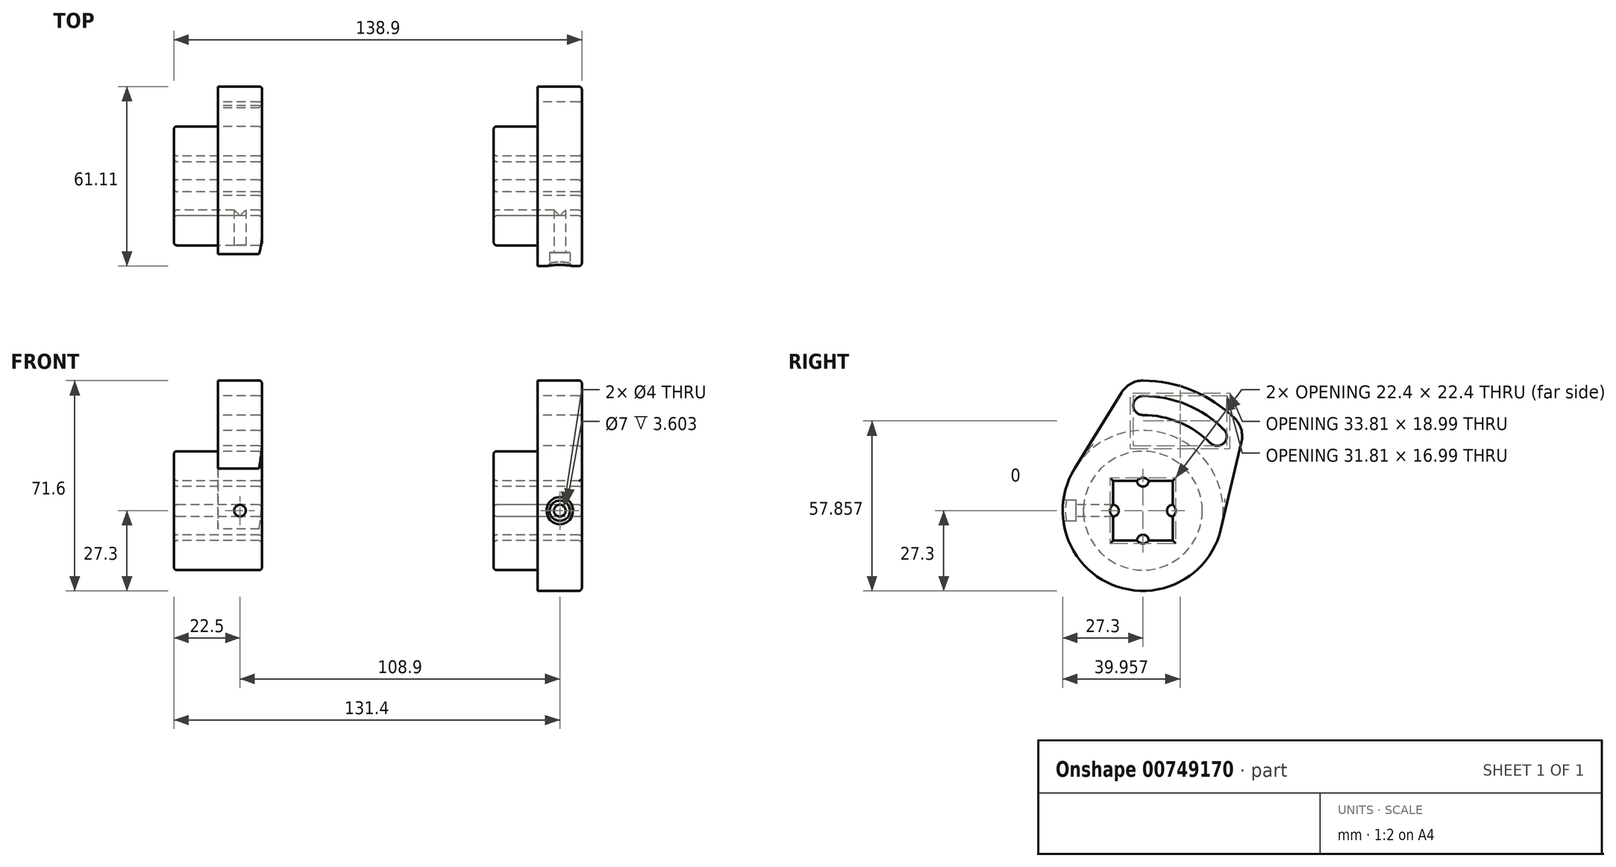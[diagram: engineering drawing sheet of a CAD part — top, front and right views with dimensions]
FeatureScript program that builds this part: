
annotation { "Feature Type Name" : "Feature", "Feature Type Description" : "" }
export const myFeature = defineFeature(function(context is Context, id is Id, definition is map)
    precondition{}
    {
        {
            var Q0;
            Q0=qCreatedBy(makeId("Right.planeOp"),FACE);
            var sketch = newSketch(context, id + "F0", { "sketchPlane" : qUnion([Q0])});
            skPoint(sketch, "E0.middle", {"position": v(0, 0) * mm});
            skCircle(sketch, "E1", {"center": v(0, 0) * mm, "radius": 20.25 * mm});
            skSolve(sketch);
        }
        {
            var Q0;
            Q0=makeQuery(id+"F0.imprint","IMPRINT",FACE,{"disambiguationData":[TD([[makeQuery(id+"F0.imprint","IMPRINT",EDGE,{"derivedFrom":sQuery(id+"F0.wireOp",EDGE,"E1")}),1.0]])]});
            extrude(context, id + "F1", {"entities" : qUnion([Q0]), "depth" : 15 * mm, "offsetDistance" : 25 * mm});
        }
        {
            var Q0;
            Q0=makeQuery(id+"F1.opExtrude","CAP_FACE",FACE,{"disambiguationData":[OSD([sQuery(id+"F0.wireOp",EDGE,"E1")])],"isStart":false});
            var sketch = newSketch(context, id + "F2", { "sketchPlane" : qUnion([Q0])});
            skPoint(sketch, "E2.center", {"position": v(0, 0) * mm});
            skArc(sketch, "E3", {"start": v(-23.23, 14.34) * mm, "mid": v(-10.45, -25.22) * mm, "end": v(26.57, -6.3) * mm});
            skArc(sketch, "E4", {"start": v(0, 44.3) * mm, "mid": v(-4.14, 43.22) * mm, "end": v(-7.23, 40.26) * mm});
            skArc(sketch, "E5", {"start": v(0, 39.05) * mm, "mid": v(-3.25, 35.8) * mm, "end": v(0, 32.55) * mm});
            skArc(sketch, "E6.1.0", {"start": v(33.59, 23.36) * mm, "mid": v(33.5, 27.63) * mm, "end": v(31.32, 31.32) * mm});
            skArc(sketch, "E6.1.1", {"start": v(23.02, 23.02) * mm, "mid": v(27.61, 23.02) * mm, "end": v(27.61, 27.61) * mm});
            skLineSegment(sketch, "E6.anchor1", {"start": v(0, 0) * mm, "end": v(0, 35.8) * mm, "construction": true});
            skLineSegment(sketch, "E6.anchor2", {"start": v(0, 0) * mm, "end": v(25.31, 25.31) * mm, "construction": true});
            skArc(sketch, "E7", {"start": v(0, 44.3) * mm, "mid": v(16.95, 40.93) * mm, "end": v(31.32, 31.32) * mm});
            skLineSegment(sketch, "E8", {"start": v(-7.23, 40.26) * mm, "end": v(-23.23, 14.34) * mm});
            skLineSegment(sketch, "E9", {"start": v(33.59, 23.36) * mm, "end": v(26.57, -6.3) * mm});
            skArc(sketch, "E10", {"start": v(0, 39.05) * mm, "mid": v(14.94, 36.08) * mm, "end": v(27.61, 27.61) * mm});
            skArc(sketch, "E11", {"start": v(0, 32.55) * mm, "mid": v(12.46, 30.07) * mm, "end": v(23.02, 23.02) * mm});
            skSolve(sketch);
        }
        {
            var Q0;
            Q0=makeQuery(id+"F2.imprint","IMPRINT",FACE,{"disambiguationData":[TD([[makeQuery(id+"F2.imprint","IMPRINT",EDGE,{"derivedFrom":sQuery(id+"F2.wireOp",EDGE,"mr3UQ9HW-HN6N-brF4-2AbY-BRYGOn4Xsbo6")}),1.0]])]});
            var Q1;
            Q1=makeQuery(id+"F2.imprint","IMPRINT",FACE,{"disambiguationData":[TD([[makeQuery(id+"F2.imprint","IMPRINT",EDGE,{"derivedFrom":makeQuery(id+"F1.opExtrude","CAP_EDGE",EDGE,{"disambiguationData":[OSD([sQuery(id+"F0.wireOp",EDGE,"E1")])],"isStart":false})}),1.0]])]});
            extrude(context, id + "F3", {"entities" : qUnion([Q0, Q1]), "operationType" : NewBodyOperationType.ADD, "depth" : 15 * mm, "offsetDistance" : 25 * mm});
        }
        {
            var Q0;
            Q0=makeQuery(id+"F1.opExtrude","CAP_FACE",FACE,{"disambiguationData":[OSD([sQuery(id+"F0.wireOp",EDGE,"E1")])],"isStart":true});
            var sketch = newSketch(context, id + "F4", { "sketchPlane" : qUnion([Q0])});
            skLineSegment(sketch, "E12.bottom", {"start": v(10.2, -10.2) * mm, "end": v(-10.2, -10.2) * mm});
            skLineSegment(sketch, "E12.top", {"start": v(10.2, 10.2) * mm, "end": v(-10.2, 10.2) * mm});
            skLineSegment(sketch, "E12.left", {"start": v(10.2, -10.2) * mm, "end": v(10.2, 10.2) * mm});
            skLineSegment(sketch, "E12.right", {"start": v(-10.2, -10.2) * mm, "end": v(-10.2, 10.2) * mm});
            skPoint(sketch, "E12.middle", {"position": v(0, 0) * mm});
            skArc(sketch, "E13", {"start": v(-2, 10.2) * mm, "mid": v(0, 8.2) * mm, "end": v(2, 10.2) * mm});
            skPoint(sketch, "E13.centerSnap0", {"position": v(0, 10.2) * mm});
            skArc(sketch, "E14.1.0", {"start": v(-10.2, -2) * mm, "mid": v(-8.2, 0) * mm, "end": v(-10.2, 2) * mm});
            skArc(sketch, "E14.2.0", {"start": v(2, -10.2) * mm, "mid": v(0, -8.2) * mm, "end": v(-2, -10.2) * mm});
            skArc(sketch, "E14.3.0", {"start": v(10.2, 2) * mm, "mid": v(8.2, 0) * mm, "end": v(10.2, -2) * mm});
            skSolve(sketch);
        }
        {
            var Q0;
            {var subQ0=sQuery(id+"F4.wireOp",EDGE,"E13");Q0=makeQuery(id+"F4.imprint","IMPRINT",FACE,{"disambiguationData":[TD([[makeQuery(id+"F4.imprint","IMPRINT",EDGE,{"derivedFrom":subQ0}),-1.0]])]});}
            extrude(context, id + "F5", {"entities" : qUnion([Q0]), "operationType" : NewBodyOperationType.REMOVE, "endBound" : BoundingType.UP_TO_NEXT, "oppositeDirection" : true, "depth" : 25 * mm, "offsetDistance" : 25 * mm});
        }
        {
            var Q0;
            Q0=makeQuery(id+"F2.imprint","IMPRINT",FACE,{"disambiguationData":[TD([[makeQuery(id+"F2.imprint","IMPRINT",EDGE,{"derivedFrom":sQuery(id+"F2.wireOp",EDGE,"E3")}),1.0]])]});
            var Q1;
            Q1=makeQuery(id+"F3.opExtrude","CAP_FACE",FACE,{"disambiguationData":[OSD([sQuery(id+"F0.wireOp",EDGE,"E1")])],"isStart":false});
            extrude(context, id + "F6", {"entities" : qUnion([Q0]), "operationType" : NewBodyOperationType.ADD, "endBound" : BoundingType.UP_TO_SURFACE, "depth" : 25 * mm, "endBoundEntityFace" : qUnion([Q1]), "offsetDistance" : 25 * mm});
        }
        {
            var Q0;
            Q0=qCreatedBy(makeId("Front.planeOp"),FACE);
            cPlane(context, id + "F7", {"entities" : qUnion([Q0]), "cplaneType" : CPlaneType.OFFSET, "offset" : 27.7 * mm, "width" : 150 * mm, "height" : 150 * mm});
        }
        {
            var Q0;
            Q0=qCreatedBy(id+"F7.planeOp",FACE);
            var sketch = newSketch(context, id + "F8", { "sketchPlane" : qUnion([Q0])});
            skCircle(sketch, "E15", {"center": v(22.5, 0) * mm, "radius": 2 * mm});
            skLineSegment(sketch, "E16", {"start": v(30, -27.3) * mm, "end": v(15, -27.3) * mm, "construction": true});
            skPoint(sketch, "E17", {"position": v(22.5, -27.3) * mm});
            skCircle(sketch, "E18", {"center": v(22.5, 0) * mm, "radius": 3.5 * mm});
            skSolve(sketch);
        }
        {
            var Q0;
            Q0=makeQuery(id+"F8.imprint","IMPRINT",FACE,{"disambiguationData":[TD([[makeQuery(id+"F8.imprint","IMPRINT",EDGE,{"derivedFrom":sQuery(id+"F8.wireOp",EDGE,"E15")}),1.0]])]});
            extrude(context, id + "F9", {"entities" : qUnion([Q0]), "operationType" : NewBodyOperationType.REMOVE, "oppositeDirection" : true, "depth" : 25 * mm, "offsetDistance" : 25 * mm});
        }
        {
            var Q0;
            Q0=makeQuery(id+"F8.imprint","IMPRINT",FACE,{"disambiguationData":[TD([[makeQuery(id+"F8.imprint","IMPRINT",EDGE,{"derivedFrom":sQuery(id+"F8.wireOp",EDGE,"E15")}),-1.0]])]});
            extrude(context, id + "F10", {"entities" : qUnion([Q0]), "operationType" : NewBodyOperationType.REMOVE, "oppositeDirection" : true, "depth" : 5 * mm, "offsetDistance" : 25 * mm});
        }
        {
            var Q0;
            Q0=makeQuery(id+"F10.boolean.opBoolean","INTERSECT",EDGE,{"derivedFrom":[makeQuery(id+"F6.opExtrude","SWEPT_FACE",FACE,{"disambiguationData":[OSD([sQuery(id+"F2.wireOp",EDGE,"E3")])]}),makeQuery(id+"F10.opExtrude","SWEPT_FACE",FACE,{"disambiguationData":[OSD([sQuery(id+"F8.wireOp",EDGE,"E18")])]})]});
            fillet(context, id + "F11", {"entities" : qUnion([Q0]), "radius" : 1 * mm, "tangentPropagation" : true, "allowEdgeOverflow" : false});
        }
        {
            var Q0;
            Q0=makeQuery(id+"F1.opExtrude","SWEPT_BODY",BODY,{"disambiguationData":[OSD([sQuery(id+"F0.wireOp",EDGE,"E1")])]});
            transform(context, id + "F12", {"entities" : qUnion([Q0]), "transformType" : TransformType.TRANSLATION_3D, "dx" : -108.9 * mm, "dy" : 0 * mm, "dz" : 0 * mm, "makeCopy" : true});
        }
        {
            var Q0;
            Q0=makeQuery(id+"F12.opPattern","COPY",FACE,{"derivedFrom":makeQuery(id+"F6.opExtrude","CAP_FACE",FACE,{"disambiguationData":[OSD([sQuery(id+"F0.wireOp",EDGE,"E1"),sQuery(id+"F2.wireOp",EDGE,"E3"),sQuery(id+"F2.wireOp",EDGE,"E4"),sQuery(id+"F2.wireOp",EDGE,"E5"),sQuery(id+"F2.wireOp",EDGE,"E6.1.0"),sQuery(id+"F2.wireOp",EDGE,"E6.1.1"),sQuery(id+"F2.wireOp",EDGE,"E7"),sQuery(id+"F2.wireOp",EDGE,"E8"),sQuery(id+"F2.wireOp",EDGE,"E9"),sQuery(id+"F2.wireOp",EDGE,"E10"),sQuery(id+"F2.wireOp",EDGE,"E11")])],"isStart":true}),"instanceName":"1"});
            var sketch = newSketch(context, id + "F13", { "sketchPlane" : qUnion([Q0])});
            skArc(sketch, "E19.0", {"start": v(23.23, 14.34) * mm, "mid": v(10.45, -25.22) * mm, "end": v(-26.57, -6.3) * mm});
            skArc(sketch, "E20", {"start": v(-26.57, -6.3) * mm, "mid": v(-10.45, 25.22) * mm, "end": v(23.23, 14.34) * mm});
            skSolve(sketch);
        }
        {
            var Q0;
            Q0=makeQuery(id+"F13.imprint","IMPRINT",FACE,{"disambiguationData":[TD([[makeQuery(id+"F13.imprint","IMPRINT",EDGE,{"derivedFrom":sQuery(id+"F13.wireOp",EDGE,"E20")}),1.0]])]});
            extrude(context, id + "F14", {"entities" : qUnion([Q0]), "operationType" : NewBodyOperationType.REMOVE, "oppositeDirection" : true, "depth" : 25 * mm, "offsetDistance" : 25 * mm});
        }
        {
            var Q0;
            {var subQ0=sQuery(id+"F0.wireOp",EDGE,"E1");Q0=makeQuery(id+"F6.boolean.opBoolean","MERGE",FACE,{"derivedFrom":[makeQuery(id+"F3.opExtrude","CAP_FACE",FACE,{"disambiguationData":[OSD([subQ0])],"isStart":false}),makeQuery(id+"F6.opExtrude","CAP_FACE",FACE,{"disambiguationData":[OSD([subQ0])],"isStart":false})]});}
            var Q1;
            Q1=makeQuery(id+"F1.opExtrude","CAP_FACE",FACE,{"disambiguationData":[OSD([sQuery(id+"F0.wireOp",EDGE,"E1")])],"isStart":true});
            var Q2;
            Q2=makeQuery(id+"F12.opPattern","COPY",EDGE,{"derivedFrom":makeQuery(id+"F1.opExtrude","CAP_EDGE",EDGE,{"disambiguationData":[OSD([sQuery(id+"F0.wireOp",EDGE,"E1")])],"isStart":true}),"instanceName":"1"});
            var Q3;
            {var subQ0=sQuery(id+"F0.wireOp",EDGE,"E1");Q3=makeQuery(id+"F14.boolean.opBoolean","INTERSECT",EDGE,{"derivedFrom":[makeQuery(id+"F12.opPattern","COPY",FACE,{"derivedFrom":makeQuery(id+"F6.boolean.opBoolean","MERGE",FACE,{"derivedFrom":[makeQuery(id+"F3.opExtrude","CAP_FACE",FACE,{"disambiguationData":[OSD([subQ0])],"isStart":false}),makeQuery(id+"F6.opExtrude","CAP_FACE",FACE,{"disambiguationData":[OSD([subQ0])],"isStart":false})]}),"instanceName":"1"}),makeQuery(id+"F14.opExtrude","SWEPT_FACE",FACE,{"disambiguationData":[OSD([sQuery(id+"F13.wireOp",EDGE,"E20")])]})]});}
            var Q4;
            {var subQ0=sQuery(id+"F0.wireOp",EDGE,"E1");Q4=makeQuery(id+"F12.opPattern","COPY",FACE,{"derivedFrom":makeQuery(id+"F6.boolean.opBoolean","MERGE",FACE,{"derivedFrom":[makeQuery(id+"F3.opExtrude","CAP_FACE",FACE,{"disambiguationData":[OSD([subQ0])],"isStart":false}),makeQuery(id+"F6.opExtrude","CAP_FACE",FACE,{"disambiguationData":[OSD([subQ0])],"isStart":false})]}),"instanceName":"1"});}
            var Q5;
            Q5=makeQuery(id+"F12.opPattern","COPY",FACE,{"derivedFrom":makeQuery(id+"F1.opExtrude","CAP_FACE",FACE,{"disambiguationData":[OSD([sQuery(id+"F0.wireOp",EDGE,"E1")])],"isStart":true}),"instanceName":"1"});
            fillet(context, id + "F15", {"entities" : qUnion([Q0, Q1, Q2, Q3, Q4, Q5]), "radius" : 1 * mm, "tangentPropagation" : true, "allowEdgeOverflow" : false});
        }
    });
